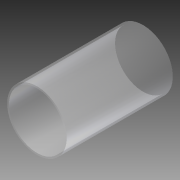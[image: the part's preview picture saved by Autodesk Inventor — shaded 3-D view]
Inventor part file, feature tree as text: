
AUTODESK INVENTOR PART (.ipt)
format: ipt  version: 2012 (Build 160160000, 160)  size: 83,456 bytes
history: native  units: mm
features: extrude x1, sketch x1
ambient origin geometry x8: Origin, YZ Plane, XZ Plane, XY Plane, X Axis, Y Axis, Z Axis, Center Point
bodies: Solid1 (feature_tree)
feature tree (2):
  extrude  "Extrusion1"  Depth=95.0mm
  sketch  "Sketch1"  dims[d0=101.0mm d1=95.0mm d2=180.0mm d3=0.0mm]
